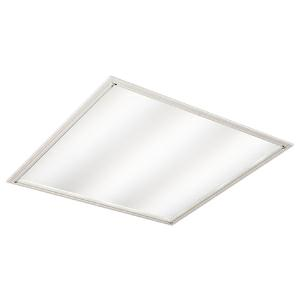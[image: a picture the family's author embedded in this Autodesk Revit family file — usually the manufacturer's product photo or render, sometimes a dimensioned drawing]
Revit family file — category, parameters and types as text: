
# Revit family: 3f_filippi_-_l_320_lgs_3f_filippi_-_21587_-_l_324x10w_led_dali_lgs_596x596
name_source: partatom
category: Lighting Fixtures
units: mm (PartAtom-declared; Revit-internal decimal feet)

## family parameters
Cut with Voids When Loaded = No
Host = Face
Light Source = No
Part Type = Normal
Room Calculation Point = No
Round Connector Dimension = Use Diameter
Shared = No

## types (1)
- 3F Filippi - L 320 LGS (1 x LED, 4292 lm, 45 W, 4000 K)
    Apparent Load = 45 VA
    Approval mark = ENEC
    CIE Flux Codes = 62 88 97 100 100
    Color Rendering = 80
    Color Temperature = 4000 K
    Control Gear = Electronic transformer
    Default Elevation = 1800 mm
    Description = ILLUMINOTECHNICAL
Luminous efficiency 100% (DLOR 100%, ULOR 0%).
Initial luminous flux of the luminaire 4292 lm.
Direct symmetric distribution.
Installation Interdistance Transv.D = 1.16 x hu - Long.D = 1.16 x hu.
Average luminance <3000 cd/m² for radial angles >65°.
Tabular UGR (CIE 117 - 4H-8H; S=0.25H; 70/50/20): RUG 18.8 - 18.8.
Beam angle: 85° - 84°.
Luminous efficacy 95 lm/W.
Lifetime (L93/B10): 30000 h. (tq+25°C)
Lifetime (L90/B10): 50000 h. (tq+25°C)
Lifetime (L85/B10): 80000 h. (tq+25°C)
Lifetime (L80/B10): 100000 h. (tq+25°C)
Sudden decreased luminous flux after 50000 hours: 0% (C0).
Photobiological safety in compliance with IEC/TR 62778: RG0 risk exempt, (IEC 62471).
In compliance with IEC/EN 62722-2-1 - IEC/EN 62717 standards.

SOURCE
4 linear LED modules 10W/840.
Energy efficiency class (UE 2019/2020 - UE 2019/2015): D.
CIE 13.3 Colour rendering index: CRI >80 (R9 <50%).
IES TM-30 Fidelity Index: Rf = 84 Rg = 95.
CCT nominal colour temperature 4000 K.
Colour initial tolerance (MacAdam): SDCM 2.

MECHANICAL
Housing in hot-galvanised steel, painted in white polyester.
Micro-prismatic flat diffuser in transparent methacrylate (PMMA), multilenticular exterior, anti-glare, locked to the white painted aluminium perimetral frame, sealing gasket, hinged opening.
Anti-glare opal polycarbonate filter for brightness uniformity.
Luminaire with limited surface temperature. - D - (EN 60598-2-24)
Dimensions: 596x596 mm, height 80 mm. Weight 4.73 kg.
IP54 protection degree for exposed part, IP20 for recessed part.
Mechanical strength to impacts IK06 (1 joule).
Glow-wire test resistance 650°C.

ELECTRICAL
Halogen Free DALI-2 DATI (Parts 251, 252, 253), PUSH-DIM, electronic wiring 230V-50/60Hz, power factor 0.95 at full load, THD <25%, constant output current, SELV, class I, 1 driver, 1 DALI addresse.
Power of the luminaire 45 W.
CE - IEC 60598-1 - EN 60598-1.
SAFE FLICKER: PstLM=<1 and SVM=<0.4 (IEC TR 61547-1 and IEC TR 63158), to ensure a more comfortable and safe light.
Luminaire compliant with EN 60598-2-22 for power supply from a centralised emergency system CPSS (Central Power Supply System), not incorporated in the luminaire - high risk areas excluded. The default power and flux are 100% in AC and 15% in DC.
Ambient temperature from 0°C to +25°C.
Temperature class T6 max 85°C.
Relative humidity UR: <85%.

INSTALLATION
Lay-in recessed fitting.
On request: pull-up recessed fitting with brackets.
False ceiling carving: 580x580 mm.
All accessories dedicated to this product are available on the Catalog and on our website www.3F-Filippi.com.

APPLICATIONS
Environments: sterilized, aseptic.
In environments with VDU's, managerial offices and staterooms, environments involving accurate visual tasks where a diffused and soft light for an optimum visual comfort and the source total shielding are required.

LIGHT MANAGEMENT
Recommended minimum setting: 10%.
The luminaire, equipped with (DALI-2 DATI) driver, can be controlled manually with 3F Easy Dim technology or automatically/manually with wired or wireless DALI/D2D control systems.
The D2D driver guarantees interoperability with other devices with the same certification by making the following information available:
Device Data (Part 251), Energy Report (Part 252), Diagnosis & Maintenance (Part 253).
In electrical systems without a regulation system (manual or automatic) and DALI bus, a suitable jumper must be made on the DA-DA terminals of the appliance.

WARNING
Luminaire designed for disposal/recycling at end-of-life.
Replaceable (LED only) light source by a professional. Replaceable control gear by a professional.
    Height = 0 mm  [stored 0 ft]
    Lamp = 1 x LED
    Lamp Light Flux = 4292 lm
    Lamp Power = 45 W
    Lamp count = 1
    Length = 596 mm
    Lifetime = 50000 h
    Luminous efficacy = 95 lm/W
    Manufacturer = 3F Filippi
    ModVariant = No
    Model = 3F Filippi - 21587 - L 324x10W LED DALI LGS 596x596
    Mounting Place = Ceiling
    Mounting Type = Recessed
    Number of Poles = 1
    OnlyDefault = Yes
    Power Factor = 1
    Product Name = 3F Filippi - L 320 LGS
    Product group = recessed luminaire
    ProductGroupID = 4
    Protection Class = Protection class I
    Protection Degree = IP 20
    RLX_Detail_Level = 1
    RLX_Emergency_Light_Flux = 0 lm
    RLX_Emergency_Type = 0
    RLX_Emergency_Type_DB = No
    RlxData = <blob elided: 36405 chars, md5=f933db6b>
    Socket = socket
    Standby Power = 0 W
    System Light Flux = 4292 lm
    System Power = 45 W
    Type Comments = Product without accessories
    Type Image = 3ffilippi_l_320_led_lgs.jpg
    URL = http://relux.com
    VarID = ---
    Voltage = 0 V
    Weight = 0.00 kg
    Width = 596 mm

note: [stored X ft] marks values corroborated as IEEE doubles in the binary element streams (Revit-internal decimal feet)

## geometry (parser evidence)
native form markers: Blend x4, Sweep x12
no freeform markers — native parametric forms only
